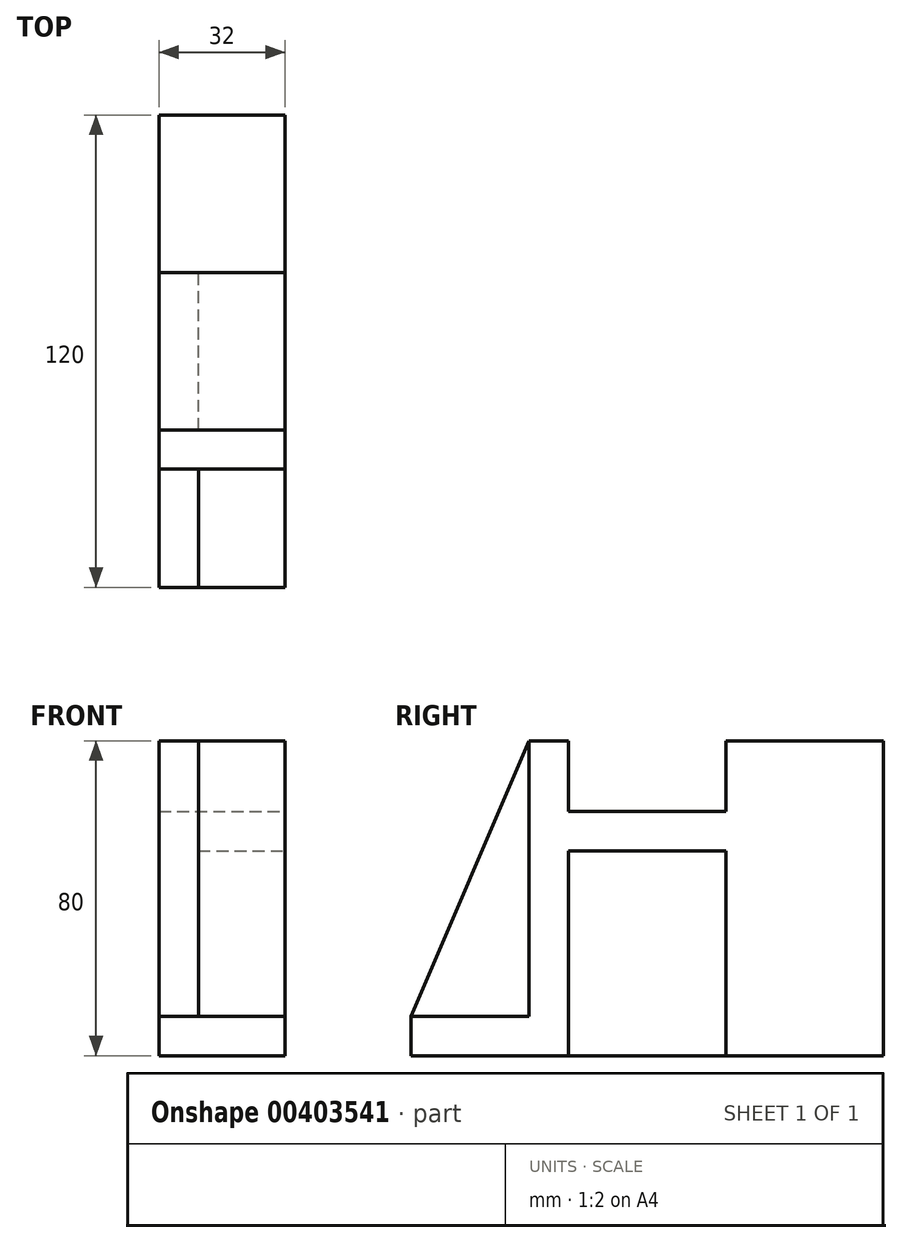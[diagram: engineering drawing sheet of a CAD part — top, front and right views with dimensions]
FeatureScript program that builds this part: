
annotation { "Feature Type Name" : "Feature", "Feature Type Description" : "" }
export const myFeature = defineFeature(function(context is Context, id is Id, definition is map)
    precondition{}
    {
        {
            var Q0;
            Q0=qCreatedBy(makeId("Right.planeOp"),FACE);
            var sketch = newSketch(context, id + "F0", { "sketchPlane" : qUnion([Q0])});
            skLineSegment(sketch, "E0.bottom", {"start": v(-60, 40) * mm, "end": v(60, 40) * mm});
            skLineSegment(sketch, "E0.top", {"start": v(-60, -40) * mm, "end": v(60, -40) * mm});
            skLineSegment(sketch, "E0.left", {"start": v(-60, 40) * mm, "end": v(-60, -40) * mm});
            skLineSegment(sketch, "E0.right", {"start": v(60, 40) * mm, "end": v(60, -40) * mm});
            skPoint(sketch, "E0.middle", {"position": v(0, 0) * mm});
            skSolve(sketch);
        }
        {
            var Q0;
            Q0 = qSketchRegion(id + "F0", true);
            extrude(context, id + "F1", {"entities" : qUnion([Q0]), "oppositeDirection" : true, "depth" : 32 * mm});
        }
        {
            var Q0;
            Q0=makeQuery(id+"F1.opExtrude","CAP_FACE",FACE,{"disambiguationData":[OSD([sQuery(id+"F0.wireOp",EDGE,"E0.bottom"),sQuery(id+"F0.wireOp",EDGE,"E0.top"),sQuery(id+"F0.wireOp",EDGE,"E0.left"),sQuery(id+"F0.wireOp",EDGE,"E0.right")])],"isStart":true});
            var sketch = newSketch(context, id + "F2", { "sketchPlane" : qUnion([Q0])});
            skLineSegment(sketch, "E1.bottom", {"start": v(-20, -40) * mm, "end": v(20, -40) * mm});
            skLineSegment(sketch, "E1.top", {"start": v(-20, 12) * mm, "end": v(20, 12) * mm});
            skLineSegment(sketch, "E1.left", {"start": v(-20, -40) * mm, "end": v(-20, 12) * mm});
            skLineSegment(sketch, "E1.right", {"start": v(20, -40) * mm, "end": v(20, 12) * mm});
            skSolve(sketch);
        }
        {
            var Q0;
            Q0 = qSketchRegion(id + "F2", true);
            extrude(context, id + "F3", {"entities" : qUnion([Q0]), "operationType" : NewBodyOperationType.REMOVE, "oppositeDirection" : true, "depth" : 22 * mm});
        }
        {
            var Q0;
            Q0=makeQuery(id+"F1.opExtrude","CAP_FACE",FACE,{"disambiguationData":[OSD([sQuery(id+"F0.wireOp",EDGE,"E0.bottom"),sQuery(id+"F0.wireOp",EDGE,"E0.top"),sQuery(id+"F0.wireOp",EDGE,"E0.left"),sQuery(id+"F0.wireOp",EDGE,"E0.right")])],"isStart":true});
            var sketch = newSketch(context, id + "F4", { "sketchPlane" : qUnion([Q0])});
            skLineSegment(sketch, "E2.bottom", {"start": v(-20, 22) * mm, "end": v(20, 22) * mm});
            skLineSegment(sketch, "E2.top", {"start": v(-20, 40) * mm, "end": v(20, 40) * mm});
            skLineSegment(sketch, "E2.left", {"start": v(-20, 22) * mm, "end": v(-20, 40) * mm});
            skLineSegment(sketch, "E2.right", {"start": v(20, 22) * mm, "end": v(20, 40) * mm});
            skSolve(sketch);
        }
        {
            var Q0;
            Q0 = qSketchRegion(id + "F4", true);
            extrude(context, id + "F5", {"entities" : qUnion([Q0]), "operationType" : NewBodyOperationType.REMOVE, "endBound" : BoundingType.THROUGH_ALL, "oppositeDirection" : true, "depth" : 25 * mm});
        }
        {
            var Q0;
            Q0=makeQuery(id+"F1.opExtrude","CAP_FACE",FACE,{"disambiguationData":[OSD([sQuery(id+"F0.wireOp",EDGE,"E0.bottom"),sQuery(id+"F0.wireOp",EDGE,"E0.top"),sQuery(id+"F0.wireOp",EDGE,"E0.left"),sQuery(id+"F0.wireOp",EDGE,"E0.right")])],"isStart":true});
            var sketch = newSketch(context, id + "F6", { "sketchPlane" : qUnion([Q0])});
            skLineSegment(sketch, "E3.bottom", {"start": v(-20, 40) * mm, "end": v(-60, 40) * mm});
            skLineSegment(sketch, "E3.top", {"start": v(-30, -30) * mm, "end": v(-60, -30) * mm});
            skLineSegment(sketch, "E3.left", {"start": v(-30, 40) * mm, "end": v(-30, -30) * mm});
            skLineSegment(sketch, "E3.right", {"start": v(-60, 40) * mm, "end": v(-60, -30) * mm});
            skSolve(sketch);
        }
        {
            var Q0;
            Q0 = qSketchRegion(id + "F6", true);
            extrude(context, id + "F7", {"entities" : qUnion([Q0]), "operationType" : NewBodyOperationType.REMOVE, "endBound" : BoundingType.THROUGH_ALL, "oppositeDirection" : true, "depth" : 25 * mm});
        }
        {
            var Q0;
            Q0=makeQuery(id+"F1.opExtrude","CAP_FACE",FACE,{"disambiguationData":[OSD([sQuery(id+"F0.wireOp",EDGE,"E0.bottom"),sQuery(id+"F0.wireOp",EDGE,"E0.top"),sQuery(id+"F0.wireOp",EDGE,"E0.left"),sQuery(id+"F0.wireOp",EDGE,"E0.right")])],"isStart":false});
            var sketch = newSketch(context, id + "F8", { "sketchPlane" : qUnion([Q0])});
            skLineSegment(sketch, "E4", {"start": v(30, 40) * mm, "end": v(60, -30) * mm});
            skLineSegment(sketch, "E5", {"start": v(60, -30) * mm, "end": v(30, -30) * mm});
            skLineSegment(sketch, "E6", {"start": v(30, -30) * mm, "end": v(30, 40) * mm});
            skSolve(sketch);
        }
        {
            var Q0;
            Q0 = qSketchRegion(id + "F8", true);
            extrude(context, id + "F9", {"entities" : qUnion([Q0]), "operationType" : NewBodyOperationType.ADD, "oppositeDirection" : true, "depth" : 10 * mm});
        }
    });
